# Revit family: 982931BW CARE 610 CF CONN 4S S B'RES SF
name_source: partatom
category: Plumbing Fixtures
revit_build: Autodesk Revit 2016 (Build: 20161004_0715(x64)
units: mm (PartAtom-declared; Revit-internal decimal feet)

## family parameters
Cut with Voids When Loaded = No
Host = Face
OmniClass Number = 23.45.05.21.11.11
OmniClass Title = Water Operated Water Closets
Part Type = Normal
Room Calculation Point = No
Round Connector Dimension = Use Diameter
Shared = No

## types (3) — shared parameters
Assembly Code = D2010110
CW Connection = Yes
HW Connection = No
Manufacturer = GWA Bathrooms & Kitchens
Material_BackRest = GWA-Acrylic-White
Material_Backrest_Mount = GWA_Metal-Stainless
Material_Base = GWA-Porcelain-White
Material_Buttons = GWA_Metal-Chrome
Material_Cistern = GWA-Porcelain-White
Material_Pipe = GWA-Acrylic-White
Material_Seat_Mount = GWA_Metal-Stainless
URL = https://www.caroma.com.au
Vent Connection = No
Waste Connection = Yes
zero-valued in all types: Default Elevation

## per-type parameters (varying)
| type | Material_Seat | Model |
| CARE 610 CF CONN 4S S B/RES SF White | GWA-Acrylic-White | 982931BW |
| CARE 610 CF CONN 4S S B/RES SF Anthracite Grey | GWA-Acrylic-AG | 982931BAG |
| CARE 610 CF CONN 4S S B/RES SF Sorrento Blue | GWA-Acrylic-SB | 982931BSB |

note: column(s) folded — value = type name in every type: Description

## geometry (parser evidence)
native form markers: Sweep x3
no freeform markers — native parametric forms only
